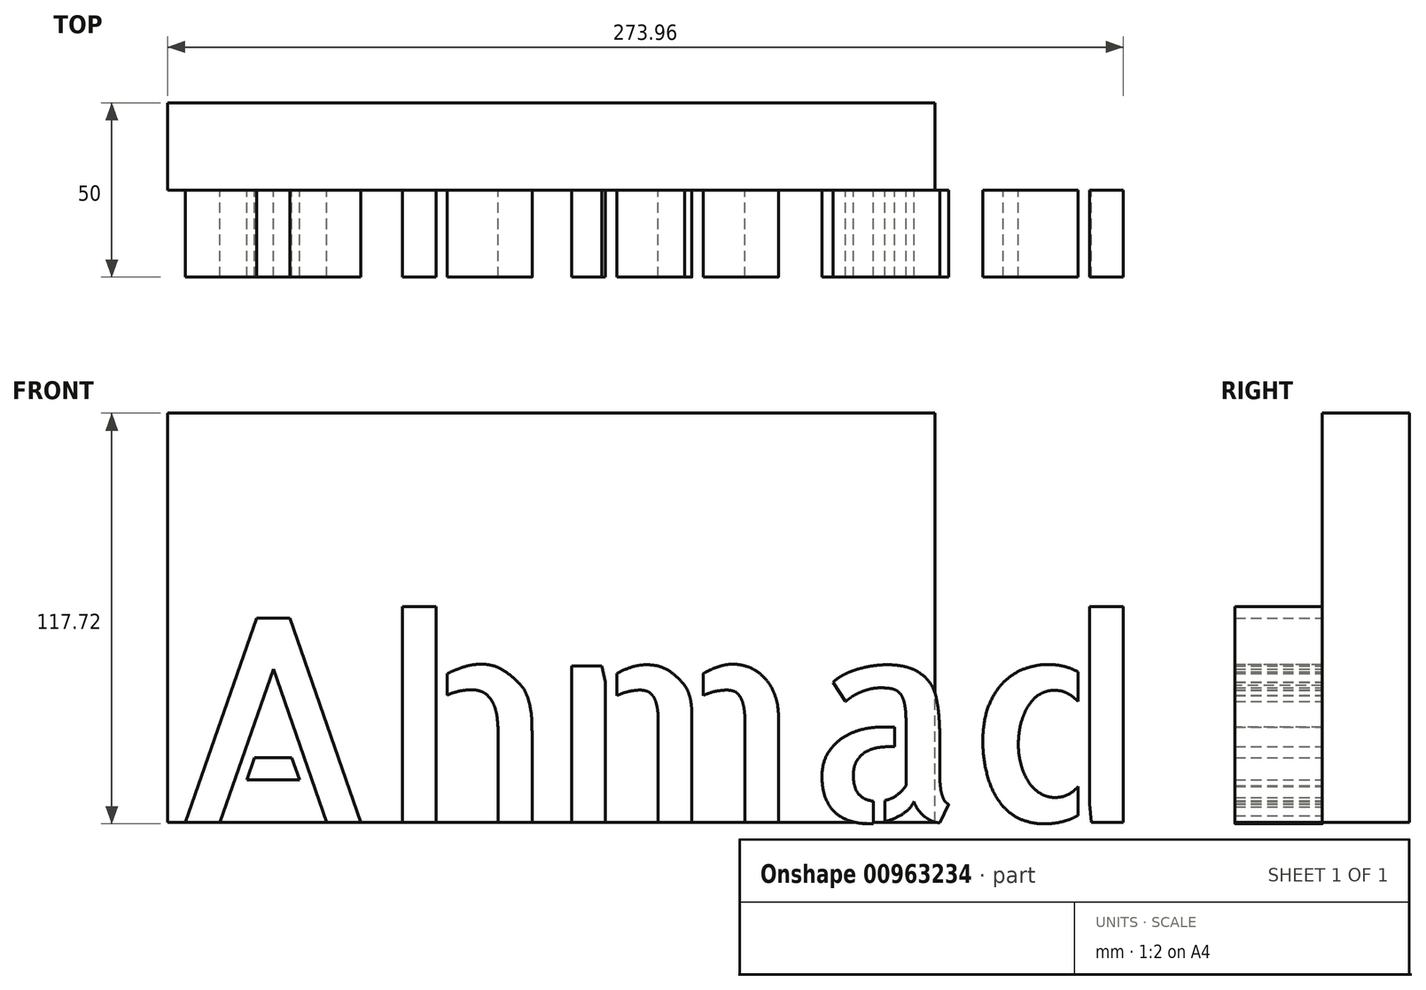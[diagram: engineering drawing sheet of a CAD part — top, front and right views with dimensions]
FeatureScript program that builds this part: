
annotation { "Feature Type Name" : "Feature", "Feature Type Description" : "" }
export const myFeature = defineFeature(function(context is Context, id is Id, definition is map)
    precondition{}
    {
        {
            var Q0;
            Q0=qCreatedBy(makeId("Front.planeOp"),FACE);
            var sketch = newSketch(context, id + "F0", { "sketchPlane" : qUnion([Q0])});
            skLineSegment(sketch, "E0.bottom", {"start": v(0, 0) * mm, "end": v(220, 0) * mm});
            skLineSegment(sketch, "E0.top", {"start": v(0, 117.33) * mm, "end": v(220, 117.33) * mm});
            skLineSegment(sketch, "E0.left", {"start": v(0, 0) * mm, "end": v(0, 117.33) * mm});
            skLineSegment(sketch, "E0.right", {"start": v(220, 0) * mm, "end": v(220, 117.33) * mm});
            skSolve(sketch);
        }
        {
            var Q0;
            Q0 = qSketchRegion(id + "F0", true);
            extrude(context, id + "F1", {"entities" : qUnion([Q0]), "depth" : 25 * mm, "offsetDistance" : 25 * mm});
        }
        {
            var Q0;
            Q0=makeQuery(id+"F1.opExtrude","CAP_FACE",FACE,{"disambiguationData":[OSD([sQuery(id+"F0.wireOp",EDGE,"E0.bottom"),sQuery(id+"F0.wireOp",EDGE,"E0.top"),sQuery(id+"F0.wireOp",EDGE,"E0.left"),sQuery(id+"F0.wireOp",EDGE,"E0.right")])],"isStart":false});
            var sketch = newSketch(context, id + "F2", { "sketchPlane" : qUnion([Q0])});
            skText(sketch, "E1", { "text": "Ahmad", "fontName": "AllertaStencil-Regular.ttf"});
            const initialGuessF2  = {"E1": [0, 0, 1, 0, 0.0587]};
            skSetInitialGuess(sketch, initialGuessF2);
            skSolve(sketch);
        }
        {
            var Q0;
            Q0 = qSketchRegion(id + "F2", true);
            extrude(context, id + "F3", {"entities" : qUnion([Q0]), "operationType" : NewBodyOperationType.ADD, "depth" : 25 * mm, "offsetDistance" : 25 * mm});
        }
    });
